AUTODESK INVENTOR PART (.ipt)
format: ipt  version: 2021 (Build 250183000, 183)  size: 187,904 bytes
history: native  units: in
note: dims shown in document units (in); Inventor stores cm internally (conversion verified against a paired STEP export)
features: sketch x4, extrude x3, fillet x3, mirror x1, hole x1, projected_geometry x1
ambient origin geometry x8: Origin, YZ Plane, XZ Plane, XY Plane, X Axis, Y Axis, Z Axis, Center Point
bodies: Solid1 (feature_tree)
feature tree (13):
  extrude  "Extrusion1"  Depth=0.1969in
  extrude  "Extrusion2"  Depth=1.4961in
  mirror  "Mirror1"
  fillet  "Fillet1"  Radius=0.126in
  hole  "Hole1"  [1 undecoded]
  fillet  "Fillet2"  [1 undecoded]
  extrude  "Extrusion3"  Depth=0.1969in
  fillet  "Fillet3"  Radius=0.5945in
  sketch  "Sketch1"  dims[d0=0.1969in d1=1.1811in]
  sketch  "Sketch2"  dims[d2=2.5591in d3=1.4961in d5=0.126in]
  projected_geometry  "Projected Loop1"
  sketch  "Sketch3"  dims[d6=0.9449in d7=0.0984in d8=30.0deg]
  sketch  "Sketch4"  dims[d9=0.1969in d10=0.1969in d11=0.5945in d12=0.0in d13=0.0787in d14=0.0in d15=0.2362in d16=1.1811in d17=0.2165in d18=0.2362in d19=0.1575in d20=0.0787in d21=90.0deg d22=0.315in d23=0.8108in d24=0.0787in d25=0.6693in d26=0.4331in d27=0.0787in d28=0.0in d29=0.0787in d30=2.3622in]
note: 2 required parameter values undecoded (feature->parameter linkage not recoverable at this tier; creation-order binding heuristic only, values carry confidence <= 0.55)
